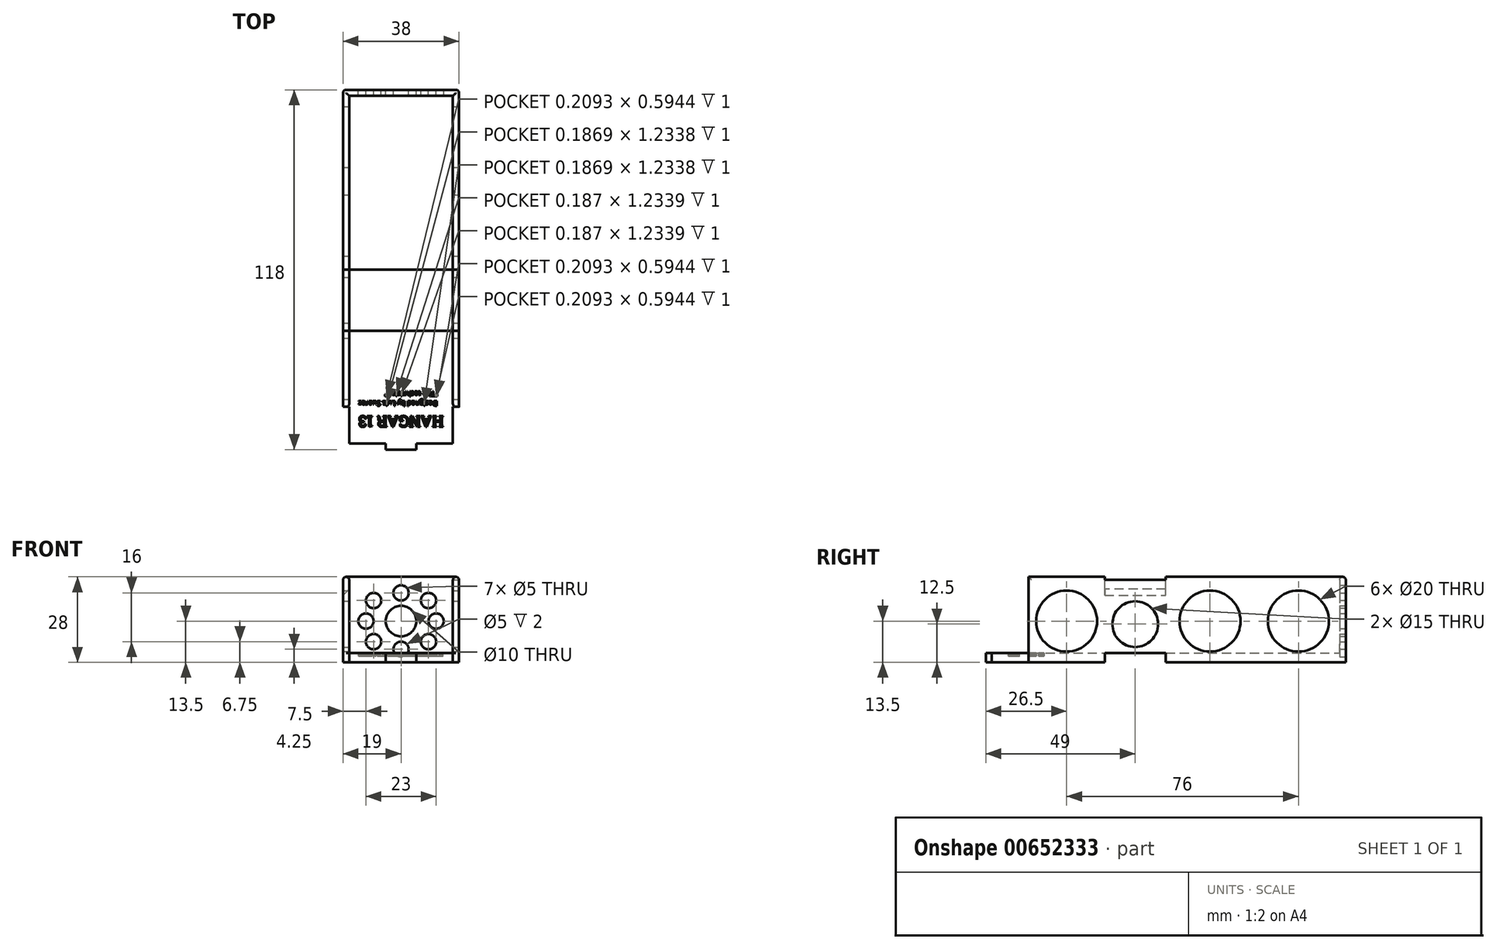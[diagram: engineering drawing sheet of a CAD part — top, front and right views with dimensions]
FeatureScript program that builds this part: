
annotation { "Feature Type Name" : "Feature", "Feature Type Description" : "" }
export const myFeature = defineFeature(function(context is Context, id is Id, definition is map)
    precondition{}
    {
        {
            var Q0;
            Q0=qCreatedBy(makeId("Top.planeOp"),FACE);
            var sketch = newSketch(context, id + "F0", { "sketchPlane" : qUnion([Q0])});
            skLineSegment(sketch, "E0.bottom", {"start": v(0, 0) * mm, "end": v(34, 0) * mm});
            skLineSegment(sketch, "E0.top", {"start": v(0, 114) * mm, "end": v(34, 114) * mm});
            skLineSegment(sketch, "E0.left", {"start": v(0, 0) * mm, "end": v(0, 114) * mm});
            skLineSegment(sketch, "E0.right", {"start": v(34, 0) * mm, "end": v(34, 114) * mm});
            skLineSegment(sketch, "E1.0", {"start": v(-2, -2) * mm, "end": v(-2, 116) * mm});
            skLineSegment(sketch, "E1.1", {"start": v(-2, -2) * mm, "end": v(36, -2) * mm});
            skLineSegment(sketch, "E1.2", {"start": v(36, -2) * mm, "end": v(36, 116) * mm});
            skLineSegment(sketch, "E1.3", {"start": v(-2, 116) * mm, "end": v(36, 116) * mm});
            skLineSegment(sketch, "E2", {"start": v(22, 0) * mm, "end": v(12, 0) * mm});
            skLineSegment(sketch, "E3", {"start": v(12, 0) * mm, "end": v(12, -2) * mm});
            skLineSegment(sketch, "E4", {"start": v(22, 0) * mm, "end": v(22, -2) * mm});
            skLineSegment(sketch, "E5", {"start": v(-2, -2) * mm, "end": v(-2, 12) * mm});
            skLineSegment(sketch, "E6", {"start": v(-2, 12) * mm, "end": v(0, 12) * mm});
            skLineSegment(sketch, "E7", {"start": v(34, 12) * mm, "end": v(36, 12) * mm});
            skSolve(sketch);
        }
        {
            var Q0;
            Q0=makeQuery(id+"F0.imprint","IMPRINT",FACE,{"disambiguationData":[TD([[makeQuery(id+"F0.imprint","IMPRINT",EDGE,{"derivedFrom":sQuery(id+"F0.wireOp",EDGE,"E0.bottom")}),-1.0]])]});
            var Q1;
            Q1=makeQuery(id+"F0.imprint","IMPRINT",FACE,{"disambiguationData":[TD([[makeQuery(id+"F0.imprint","IMPRINT",EDGE,{"derivedFrom":sQuery(id+"F0.wireOp",EDGE,"E0.bottom")}),1.0]])]});
            var Q2;
            {var subQ1=sQuery(id+"F0.wireOp",EDGE,"E0.top");Q2=makeQuery(id+"F0.imprint","IMPRINT",FACE,{"disambiguationData":[TD([[makeQuery(id+"F0.imprint","IMPRINT",EDGE,{"derivedFrom":subQ1}),1.0]])]});}
            var Q3;
            Q3=makeQuery(id+"F0.imprint","IMPRINT",FACE,{"disambiguationData":[TD([[makeQuery(id+"F0.imprint","IMPRINT",EDGE,{"derivedFrom":sQuery(id+"F0.wireOp",EDGE,"E2")}),1.0]])]});
            extrude(context, id + "F1", {"entities" : qUnion([Q0, Q1, Q2, Q3]), "oppositeDirection" : true, "depth" : 3 * mm, "offsetDistance" : 25 * mm});
        }
        {
            var Q0;
            {var subQ1=sQuery(id+"F0.wireOp",EDGE,"E0.top");Q0=makeQuery(id+"F0.imprint","IMPRINT",FACE,{"disambiguationData":[TD([[makeQuery(id+"F0.imprint","IMPRINT",EDGE,{"derivedFrom":subQ1}),1.0]])]});}
            var Q1;
            Q1=makeQuery(id+"F0.imprint","IMPRINT",FACE,{"disambiguationData":[TD([[makeQuery(id+"F0.imprint","IMPRINT",EDGE,{"derivedFrom":sQuery(id+"F0.wireOp",EDGE,"E2")}),1.0]])]});
            extrude(context, id + "F2", {"entities" : qUnion([Q0, Q1]), "depth" : 25 * mm, "offsetDistance" : 25 * mm});
        }
        {
            var Q0;
            Q0=makeQuery(id+"F2.opExtrude","SWEPT_BODY",BODY,{"disambiguationData":[OSD([sQuery(id+"F0.wireOp",EDGE,"E1.1"),sQuery(id+"F0.wireOp",EDGE,"E2"),sQuery(id+"F0.wireOp",EDGE,"E3"),sQuery(id+"F0.wireOp",EDGE,"E4")])]});
            var Q1;
            Q1=makeQuery(id+"F2.opExtrude","SWEPT_BODY",BODY,{"disambiguationData":[OSD([sQuery(id+"F0.wireOp",EDGE,"E0.top"),sQuery(id+"F0.wireOp",EDGE,"E0.left"),sQuery(id+"F0.wireOp",EDGE,"E0.right"),sQuery(id+"F0.wireOp",EDGE,"E1.0"),sQuery(id+"F0.wireOp",EDGE,"E1.2"),sQuery(id+"F0.wireOp",EDGE,"E1.3"),sQuery(id+"F0.wireOp",EDGE,"E6"),sQuery(id+"F0.wireOp",EDGE,"E7")])]});
            var Q2;
            Q2=makeQuery(id+"F1.opExtrude","SWEPT_BODY",BODY,{"disambiguationData":[OSD([sQuery(id+"F0.wireOp",EDGE,"E1.0"),sQuery(id+"F0.wireOp",EDGE,"E1.1"),sQuery(id+"F0.wireOp",EDGE,"E1.2"),sQuery(id+"F0.wireOp",EDGE,"E1.3"),sQuery(id+"F0.wireOp",EDGE,"E5")])]});
            booleanBodies(context, id + "F3", {"operationType" : BooleanOperationType.UNION, "tools" : qUnion([Q0, Q1, Q2])});
        }
        {
            var Q0;
            {var subQ0=sQuery(id+"F0.wireOp",EDGE,"E1.2");Q0=makeQuery(id+"F3.opBoolean","MERGE",FACE,{"derivedFrom":[makeQuery(id+"F1.opExtrude","SWEPT_FACE",FACE,{"disambiguationData":[OSD([subQ0])]}),makeQuery(id+"F2.opExtrude","SWEPT_FACE",FACE,{"disambiguationData":[OSD([subQ0])]})]});}
            var sketch = newSketch(context, id + "F4", { "sketchPlane" : qUnion([Q0])});
            skLineSegment(sketch, "E8.bottom", {"start": v(57, -3) * mm, "end": v(37, -3) * mm});
            skLineSegment(sketch, "E8.top", {"start": v(57, 0) * mm, "end": v(37, 0) * mm});
            skLineSegment(sketch, "E8.left", {"start": v(57, -3) * mm, "end": v(57, 0) * mm});
            skLineSegment(sketch, "E8.right", {"start": v(37, -3) * mm, "end": v(37, 0) * mm});
            skLineSegment(sketch, "E9.bottom", {"start": v(37, 25) * mm, "end": v(57, 25) * mm});
            skLineSegment(sketch, "E9.top", {"start": v(37, 24) * mm, "end": v(57, 24) * mm});
            skLineSegment(sketch, "E9.left", {"start": v(37, 25) * mm, "end": v(37, 24) * mm});
            skLineSegment(sketch, "E9.right", {"start": v(57, 25) * mm, "end": v(57, 24) * mm});
            skSolve(sketch);
        }
        {
            var Q0;
            Q0 = qSketchRegion(id + "F4", true);
            extrude(context, id + "F5", {"entities" : qUnion([Q0]), "operationType" : NewBodyOperationType.REMOVE, "endBound" : BoundingType.THROUGH_ALL, "oppositeDirection" : true, "depth" : 25 * mm, "offsetDistance" : 25 * mm});
        }
        {
            var Q0;
            Q0=makeQuery(id+"F5.boolean.opBoolean","COPY",EDGE,{"derivedFrom":makeQuery(id+"F5.opExtrude","CAP_EDGE",EDGE,{"disambiguationData":[OSD([sQuery(id+"F4.wireOp",EDGE,"E9.top")])],"isStart":true})});
            var Q1;
            {var subQ0=sQuery(id+"F0.wireOp",EDGE,"E1.0");Q1=makeQuery(id+"F5.boolean.opBoolean","INTERSECT",EDGE,{"derivedFrom":[makeQuery(id+"F3.opBoolean","MERGE",FACE,{"derivedFrom":[makeQuery(id+"F1.opExtrude","SWEPT_FACE",FACE,{"disambiguationData":[OSD([subQ0,sQuery(id+"F0.wireOp",EDGE,"E5")])]}),makeQuery(id+"F2.opExtrude","SWEPT_FACE",FACE,{"disambiguationData":[OSD([subQ0])]})]}),makeQuery(id+"F5.opExtrude","SWEPT_FACE",FACE,{"disambiguationData":[OSD([sQuery(id+"F4.wireOp",EDGE,"E9.top")])]})]});}
            chamfer(context, id + "F6", {"entities" : qUnion([Q0, Q1]), "width" : 5 * mm, "tangentPropagation" : true});
        }
        {
            var Q0;
            Q0=makeQuery(id+"F2.opExtrude","SWEPT_EDGE",EDGE,{"disambiguationData":[OSD([sQuery(id+"F0.wireOp",EDGE,"E0.left"),sQuery(id+"F0.wireOp",EDGE,"E6")])]});
            var Q1;
            Q1=makeQuery(id+"F2.opExtrude","SWEPT_EDGE",EDGE,{"disambiguationData":[OSD([sQuery(id+"F0.wireOp",EDGE,"E0.right"),sQuery(id+"F0.wireOp",EDGE,"E7")])]});
            var Q2;
            Q2=makeQuery(id+"F2.opExtrude","SWEPT_EDGE",EDGE,{"disambiguationData":[OSD([sQuery(id+"F0.wireOp",EDGE,"E0.bottom"),sQuery(id+"F0.wireOp",EDGE,"E2"),sQuery(id+"F0.wireOp",EDGE,"E3")])]});
            var Q3;
            Q3=makeQuery(id+"F2.opExtrude","SWEPT_EDGE",EDGE,{"disambiguationData":[OSD([sQuery(id+"F0.wireOp",EDGE,"E0.bottom"),sQuery(id+"F0.wireOp",EDGE,"E2"),sQuery(id+"F0.wireOp",EDGE,"E4")])]});
            var Q4;
            {var subQ0=sQuery(id+"F0.wireOp",EDGE,"E6");var subQ1=sQuery(id+"F0.wireOp",EDGE,"E0.left");Q4=makeQuery(id+"F5.boolean.opBoolean","SPLIT",EDGE,{"disambiguationData":[TD([makeQuery(id+"F2.opExtrude","SWEPT_FACE",FACE,{"disambiguationData":[OSD([subQ0])]})])],"derivedFrom":makeQuery(id+"F2.opExtrude","CAP_EDGE",EDGE,{"disambiguationData":[OSD([subQ1])],"isStart":false})});}
            var Q5;
            {var subQ0=sQuery(id+"F0.wireOp",EDGE,"E0.top");var subQ1=sQuery(id+"F0.wireOp",EDGE,"E0.left");Q5=makeQuery(id+"F5.boolean.opBoolean","SPLIT",EDGE,{"disambiguationData":[TD([makeQuery(id+"F2.opExtrude","SWEPT_FACE",FACE,{"disambiguationData":[OSD([subQ0])]})])],"derivedFrom":makeQuery(id+"F2.opExtrude","CAP_EDGE",EDGE,{"disambiguationData":[OSD([subQ1])],"isStart":false})});}
            var Q6;
            {var subQ0=sQuery(id+"F0.wireOp",EDGE,"E0.top");var subQ1=sQuery(id+"F0.wireOp",EDGE,"E0.right");Q6=makeQuery(id+"F5.boolean.opBoolean","SPLIT",EDGE,{"disambiguationData":[TD([makeQuery(id+"F2.opExtrude","SWEPT_FACE",FACE,{"disambiguationData":[OSD([subQ0])]})])],"derivedFrom":makeQuery(id+"F2.opExtrude","CAP_EDGE",EDGE,{"disambiguationData":[OSD([subQ1])],"isStart":false})});}
            var Q7;
            {var subQ0=sQuery(id+"F0.wireOp",EDGE,"E7");var subQ1=sQuery(id+"F0.wireOp",EDGE,"E0.right");Q7=makeQuery(id+"F5.boolean.opBoolean","SPLIT",EDGE,{"disambiguationData":[TD([makeQuery(id+"F2.opExtrude","SWEPT_FACE",FACE,{"disambiguationData":[OSD([subQ0])]})])],"derivedFrom":makeQuery(id+"F2.opExtrude","CAP_EDGE",EDGE,{"disambiguationData":[OSD([subQ1])],"isStart":false})});}
            var Q8;
            Q8=makeQuery(id+"F2.opExtrude","CAP_EDGE",EDGE,{"disambiguationData":[OSD([sQuery(id+"F0.wireOp",EDGE,"E0.top")])],"isStart":false});
            var Q9;
            {var subQ0=sQuery(id+"F0.wireOp",EDGE,"E1.3");var subQ1=sQuery(id+"F0.wireOp",EDGE,"E1.2");Q9=makeQuery(id+"F3.opBoolean","MERGE",EDGE,{"derivedFrom":[makeQuery(id+"F1.opExtrude","SWEPT_EDGE",EDGE,{"disambiguationData":[OSD([subQ1,subQ0])]}),makeQuery(id+"F2.opExtrude","SWEPT_EDGE",EDGE,{"disambiguationData":[OSD([subQ1,subQ0])]})]});}
            var Q10;
            {var subQ0=sQuery(id+"F0.wireOp",EDGE,"E1.3");var subQ1=sQuery(id+"F0.wireOp",EDGE,"E1.0");Q10=makeQuery(id+"F3.opBoolean","MERGE",EDGE,{"derivedFrom":[makeQuery(id+"F1.opExtrude","SWEPT_EDGE",EDGE,{"disambiguationData":[OSD([subQ1,subQ0])]}),makeQuery(id+"F2.opExtrude","SWEPT_EDGE",EDGE,{"disambiguationData":[OSD([subQ1,subQ0])]})]});}
            var Q11;
            {var subQ0=sQuery(id+"F0.wireOp",EDGE,"E1.3");var subQ1=sQuery(id+"F0.wireOp",EDGE,"E1.2");Q11=makeQuery(id+"F5.boolean.opBoolean","SPLIT",EDGE,{"disambiguationData":[TD([makeQuery(id+"F1.opExtrude","SWEPT_FACE",FACE,{"disambiguationData":[OSD([subQ0])]})])],"derivedFrom":makeQuery(id+"F2.opExtrude","CAP_EDGE",EDGE,{"disambiguationData":[OSD([subQ1])],"isStart":false})});}
            var Q12;
            {var subQ0=sQuery(id+"F0.wireOp",EDGE,"E7");var subQ1=sQuery(id+"F0.wireOp",EDGE,"E1.2");Q12=makeQuery(id+"F5.boolean.opBoolean","SPLIT",EDGE,{"disambiguationData":[TD([makeQuery(id+"F2.opExtrude","SWEPT_FACE",FACE,{"disambiguationData":[OSD([subQ0])]})])],"derivedFrom":makeQuery(id+"F2.opExtrude","CAP_EDGE",EDGE,{"disambiguationData":[OSD([subQ1])],"isStart":false})});}
            var Q13;
            {var subQ0=sQuery(id+"F0.wireOp",EDGE,"E1.0");var subQ1=sQuery(id+"F0.wireOp",EDGE,"E1.3");Q13=makeQuery(id+"F5.boolean.opBoolean","SPLIT",EDGE,{"disambiguationData":[TD([makeQuery(id+"F1.opExtrude","SWEPT_FACE",FACE,{"disambiguationData":[OSD([subQ1])]})])],"derivedFrom":makeQuery(id+"F2.opExtrude","CAP_EDGE",EDGE,{"disambiguationData":[OSD([subQ0])],"isStart":false})});}
            var Q14;
            {var subQ0=sQuery(id+"F0.wireOp",EDGE,"E6");var subQ1=sQuery(id+"F0.wireOp",EDGE,"E1.0");Q14=makeQuery(id+"F5.boolean.opBoolean","SPLIT",EDGE,{"disambiguationData":[TD([makeQuery(id+"F2.opExtrude","SWEPT_FACE",FACE,{"disambiguationData":[OSD([subQ0])]})])],"derivedFrom":makeQuery(id+"F2.opExtrude","CAP_EDGE",EDGE,{"disambiguationData":[OSD([subQ1])],"isStart":false})});}
            var Q15;
            Q15=makeQuery(id+"F2.opExtrude","CAP_EDGE",EDGE,{"disambiguationData":[OSD([sQuery(id+"F0.wireOp",EDGE,"E1.3")])],"isStart":false});
            var Q16;
            Q16=makeQuery(id+"F2.opExtrude","CAP_EDGE",EDGE,{"disambiguationData":[OSD([sQuery(id+"F0.wireOp",EDGE,"E2")])],"isStart":false});
            fillet(context, id + "F7", {"entities" : qUnion([Q0, Q1, Q2, Q3, Q4, Q5, Q6, Q7, Q8, Q9, Q10, Q11, Q12, Q13, Q14, Q15, Q16]), "radius" : 1 * mm, "tangentPropagation" : true, "allowEdgeOverflow" : false});
        }
        {
            var Q0;
            {var subQ0=sQuery(id+"F0.wireOp",EDGE,"E1.1");var subQ1=sQuery(id+"F0.wireOp",EDGE,"E1.0");var subQ2=sQuery(id+"F0.wireOp",EDGE,"E1.2");var subQ3=sQuery(id+"F0.wireOp",EDGE,"E5");Q0=makeQuery(id+"F5.boolean.opBoolean","SPLIT",FACE,{"disambiguationData":[TD([makeQuery(id+"F1.opExtrude","SWEPT_FACE",FACE,{"disambiguationData":[OSD([subQ0])]})])],"derivedFrom":makeQuery(id+"F1.opExtrude","CAP_FACE",FACE,{"disambiguationData":[OSD([subQ1,subQ0,subQ2,sQuery(id+"F0.wireOp",EDGE,"E1.3"),subQ3])],"isStart":true})});}
            var sketch = newSketch(context, id + "F8", { "sketchPlane" : qUnion([Q0])});
            skText(sketch, "E10", { "text": "HANGAR 13", "fontName": "RobotoSlab-Regular.ttf"});
            skText(sketch, "E11", { "text": "Designed by Luis Suarez\n\"The technician\"", "fontName": "OpenSans-Regular.ttf"});
            const initialGuessF8  = {"E10": [0.031, 0.00903, -1, 0, 0.00363], "E11": [0.029, 0.014, -1, 0, 0.00166]};
            skSetInitialGuess(sketch, initialGuessF8);
            skSolve(sketch);
        }
        {
            var Q0;
            Q0 = qSketchRegion(id + "F8", true);
            extrude(context, id + "F9", {"entities" : qUnion([Q0]), "operationType" : NewBodyOperationType.REMOVE, "oppositeDirection" : true, "depth" : 1 * mm, "offsetDistance" : 25 * mm});
        }
        {
            var Q0;
            {var subQ0=sQuery(id+"F0.wireOp",EDGE,"E1.2");Q0=makeQuery(id+"F3.opBoolean","MERGE",FACE,{"derivedFrom":[makeQuery(id+"F1.opExtrude","SWEPT_FACE",FACE,{"disambiguationData":[OSD([subQ0])]}),makeQuery(id+"F2.opExtrude","SWEPT_FACE",FACE,{"disambiguationData":[OSD([subQ0])]})]});}
            var sketch = newSketch(context, id + "F10", { "sketchPlane" : qUnion([Q0])});
            skCircle(sketch, "E12", {"center": v(24.5, 10.5) * mm, "radius": 10 * mm});
            skCircle(sketch, "E13", {"center": v(71.5, 10.5) * mm, "radius": 10 * mm});
            skCircle(sketch, "E14", {"center": v(100.5, 10.5) * mm, "radius": 10 * mm});
            skCircle(sketch, "E15", {"center": v(47, 9.5) * mm, "radius": 7.5 * mm});
            skSolve(sketch);
        }
        {
            var Q0;
            Q0 = qSketchRegion(id + "F10", true);
            extrude(context, id + "F11", {"entities" : qUnion([Q0]), "operationType" : NewBodyOperationType.REMOVE, "endBound" : BoundingType.THROUGH_ALL, "oppositeDirection" : true, "depth" : 25 * mm, "offsetDistance" : 25 * mm});
        }
        {
            var Q0;
            {var subQ0=sQuery(id+"F0.wireOp",EDGE,"E1.3");Q0=makeQuery(id+"F3.opBoolean","MERGE",FACE,{"derivedFrom":[makeQuery(id+"F1.opExtrude","SWEPT_FACE",FACE,{"disambiguationData":[OSD([subQ0])]}),makeQuery(id+"F2.opExtrude","SWEPT_FACE",FACE,{"disambiguationData":[OSD([subQ0])]})]});}
            var sketch = newSketch(context, id + "F12", { "sketchPlane" : qUnion([Q0])});
            skLineSegment(sketch, "E16", {"start": v(1, -3) * mm, "end": v(-35, 24) * mm});
            skLineSegment(sketch, "E17", {"start": v(-35, -3) * mm, "end": v(1, 24) * mm});
            skLineSegment(sketch, "E18", {"start": v(-17, 10.5) * mm, "end": v(1, -3) * mm});
            skCircle(sketch, "E19", {"center": v(-8, 3.75) * mm, "radius": 2.5 * mm});
            skCircle(sketch, "E20", {"center": v(-17, 10.5) * mm, "radius": 5 * mm});
            skLineSegment(sketch, "E21", {"start": v(-17, 10.5) * mm, "end": v(-35, -3) * mm});
            skLineSegment(sketch, "E22", {"start": v(-17, 10.5) * mm, "end": v(-35, 24) * mm});
            skLineSegment(sketch, "E23", {"start": v(-17, 10.5) * mm, "end": v(1, 24) * mm});
            skCircle(sketch, "E24", {"center": v(-8, 17.25) * mm, "radius": 2.5 * mm});
            skCircle(sketch, "E25", {"center": v(-26, 17.25) * mm, "radius": 2.5 * mm});
            skCircle(sketch, "E26", {"center": v(-26, 3.75) * mm, "radius": 2.5 * mm});
            skLineSegment(sketch, "E27", {"start": v(-35, 10.5) * mm, "end": v(-22, 10.5) * mm});
            skLineSegment(sketch, "E28", {"start": v(1, 10.5) * mm, "end": v(-12, 10.5) * mm});
            skCircle(sketch, "E29", {"center": v(-28.5, 10.5) * mm, "radius": 2.5 * mm});
            skCircle(sketch, "E30", {"center": v(-5.5, 10.5) * mm, "radius": 2.5 * mm});
            skLineSegment(sketch, "E31", {"start": v(-17, 24) * mm, "end": v(-17, 15.5) * mm});
            skLineSegment(sketch, "E32", {"start": v(-17, -3) * mm, "end": v(-17, 5.5) * mm});
            skCircle(sketch, "E33", {"center": v(-17, 1.25) * mm, "radius": 2.5 * mm});
            skCircle(sketch, "E34", {"center": v(-17, 19.75) * mm, "radius": 2.5 * mm});
            skSolve(sketch);
        }
        {
            var Q0;
            Q0 = qSketchRegion(id + "F12", true);
            extrude(context, id + "F13", {"entities" : qUnion([Q0]), "operationType" : NewBodyOperationType.REMOVE, "oppositeDirection" : true, "depth" : 2 * mm, "offsetDistance" : 25 * mm});
        }
    });
